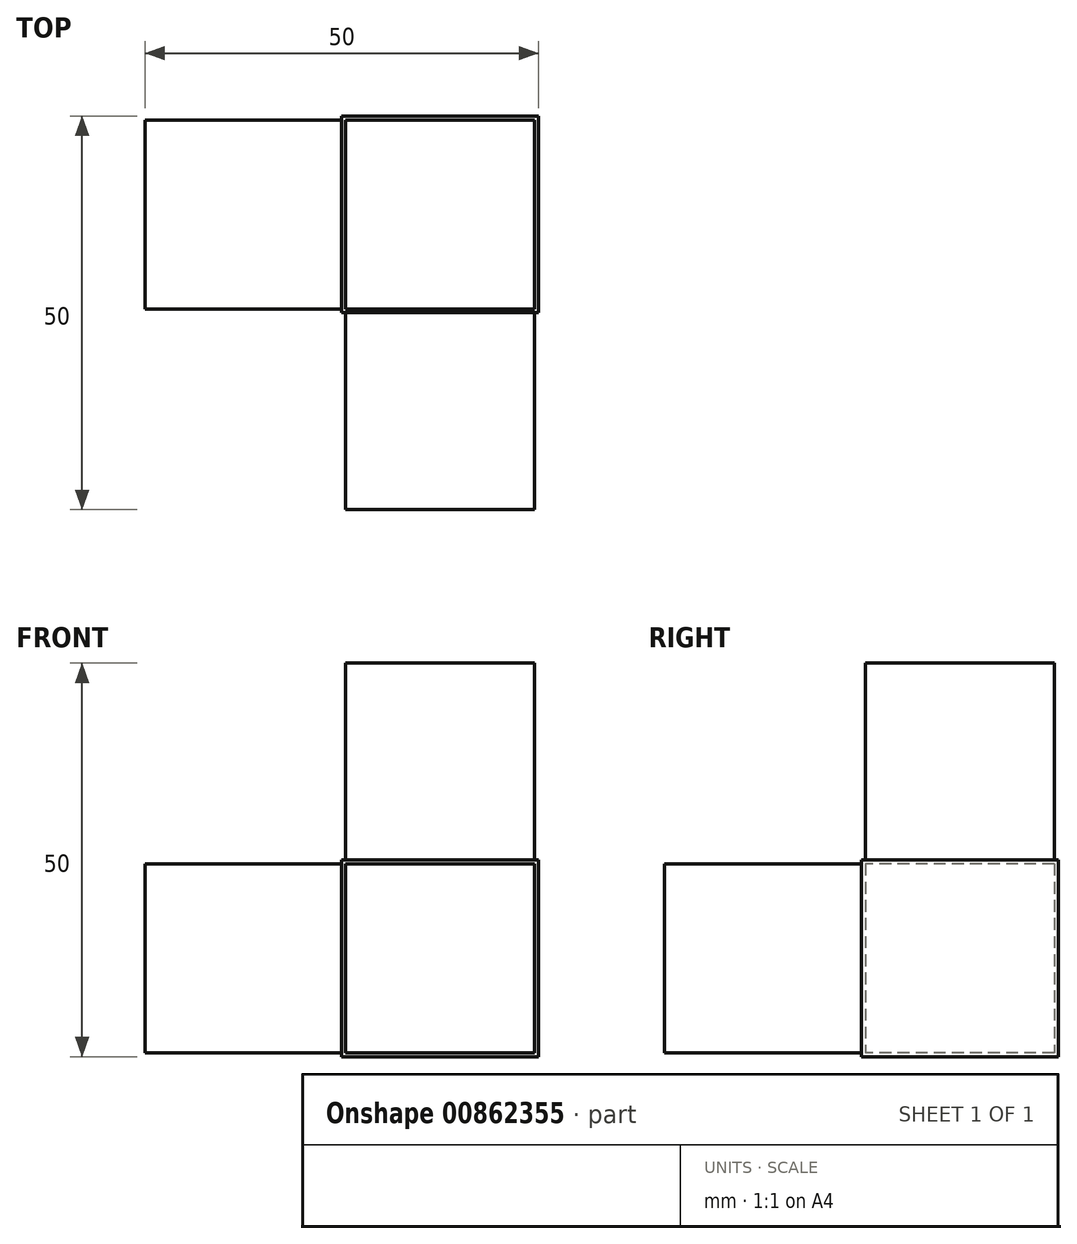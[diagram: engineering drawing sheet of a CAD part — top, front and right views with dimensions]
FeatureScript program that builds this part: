
annotation { "Feature Type Name" : "Feature", "Feature Type Description" : "" }
export const myFeature = defineFeature(function(context is Context, id is Id, definition is map)
    precondition{}
    {
        {
            var Q0;
            Q0=qCreatedBy(makeId("Right.planeOp"),FACE);
            var sketch = newSketch(context, id + "F0", { "sketchPlane" : qUnion([Q0])});
            skLineSegment(sketch, "E0.bottom", {"start": v(0, 0) * mm, "end": v(25, 0) * mm});
            skLineSegment(sketch, "E0.top", {"start": v(0, 25) * mm, "end": v(25, 25) * mm});
            skLineSegment(sketch, "E0.left", {"start": v(0, 0) * mm, "end": v(0, 25) * mm});
            skLineSegment(sketch, "E0.right", {"start": v(25, 0) * mm, "end": v(25, 25) * mm});
            skSolve(sketch);
        }
        {
            var Q0;
            Q0 = qSketchRegion(id + "F0", true);
            extrude(context, id + "F1", {"entities" : qUnion([Q0]), "depth" : 25 * mm, "offsetDistance" : 25 * mm});
        }
        {
            var Q0;
            Q0=qCreatedBy(makeId("Right.planeOp"),FACE);
            var sketch = newSketch(context, id + "F2", { "sketchPlane" : qUnion([Q0])});
            skLineSegment(sketch, "E1.bottom", {"start": v(24.5, 24.5) * mm, "end": v(0.5, 24.5) * mm});
            skLineSegment(sketch, "E1.top", {"start": v(24.5, 0.5) * mm, "end": v(0.5, 0.5) * mm});
            skLineSegment(sketch, "E1.left", {"start": v(24.5, 24.5) * mm, "end": v(24.5, 0.5) * mm});
            skLineSegment(sketch, "E1.right", {"start": v(0.5, 24.5) * mm, "end": v(0.5, 0.5) * mm});
            skSolve(sketch);
        }
        {
            var Q0;
            Q0 = qSketchRegion(id + "F2", true);
            extrude(context, id + "F3", {"entities" : qUnion([Q0]), "operationType" : NewBodyOperationType.ADD, "oppositeDirection" : true, "depth" : 25 * mm, "offsetDistance" : 25 * mm});
        }
        {
            var Q0;
            Q0=makeQuery(id+"F1.opExtrude","SWEPT_FACE",FACE,{"disambiguationData":[OSD([sQuery(id+"F0.wireOp",EDGE,"E0.left")])]});
            var sketch = newSketch(context, id + "F4", { "sketchPlane" : qUnion([Q0])});
            skLineSegment(sketch, "E2.bottom", {"start": v(0.5, 0.5) * mm, "end": v(24.5, 0.5) * mm});
            skLineSegment(sketch, "E2.top", {"start": v(0.5, 24.5) * mm, "end": v(24.5, 24.5) * mm});
            skLineSegment(sketch, "E2.left", {"start": v(0.5, 0.5) * mm, "end": v(0.5, 24.5) * mm});
            skLineSegment(sketch, "E2.right", {"start": v(24.5, 0.5) * mm, "end": v(24.5, 24.5) * mm});
            skSolve(sketch);
        }
        {
            var Q0;
            Q0 = qSketchRegion(id + "F4", true);
            extrude(context, id + "F5", {"entities" : qUnion([Q0]), "operationType" : NewBodyOperationType.ADD, "depth" : 25 * mm, "offsetDistance" : 25 * mm});
        }
        {
            var Q0;
            Q0=makeQuery(id+"F1.opExtrude","SWEPT_FACE",FACE,{"disambiguationData":[OSD([sQuery(id+"F0.wireOp",EDGE,"E0.top")])]});
            var sketch = newSketch(context, id + "F6", { "sketchPlane" : qUnion([Q0])});
            skLineSegment(sketch, "E3.bottom", {"start": v(0.5, 24.5) * mm, "end": v(24.5, 24.5) * mm});
            skLineSegment(sketch, "E3.top", {"start": v(0.5, 0.5) * mm, "end": v(24.5, 0.5) * mm});
            skLineSegment(sketch, "E3.left", {"start": v(0.5, 24.5) * mm, "end": v(0.5, 0.5) * mm});
            skLineSegment(sketch, "E3.right", {"start": v(24.5, 24.5) * mm, "end": v(24.5, 0.5) * mm});
            skSolve(sketch);
        }
        {
            var Q0;
            Q0 = qSketchRegion(id + "F6", true);
            extrude(context, id + "F7", {"entities" : qUnion([Q0]), "operationType" : NewBodyOperationType.ADD, "depth" : 25 * mm, "offsetDistance" : 25 * mm});
        }
    });
